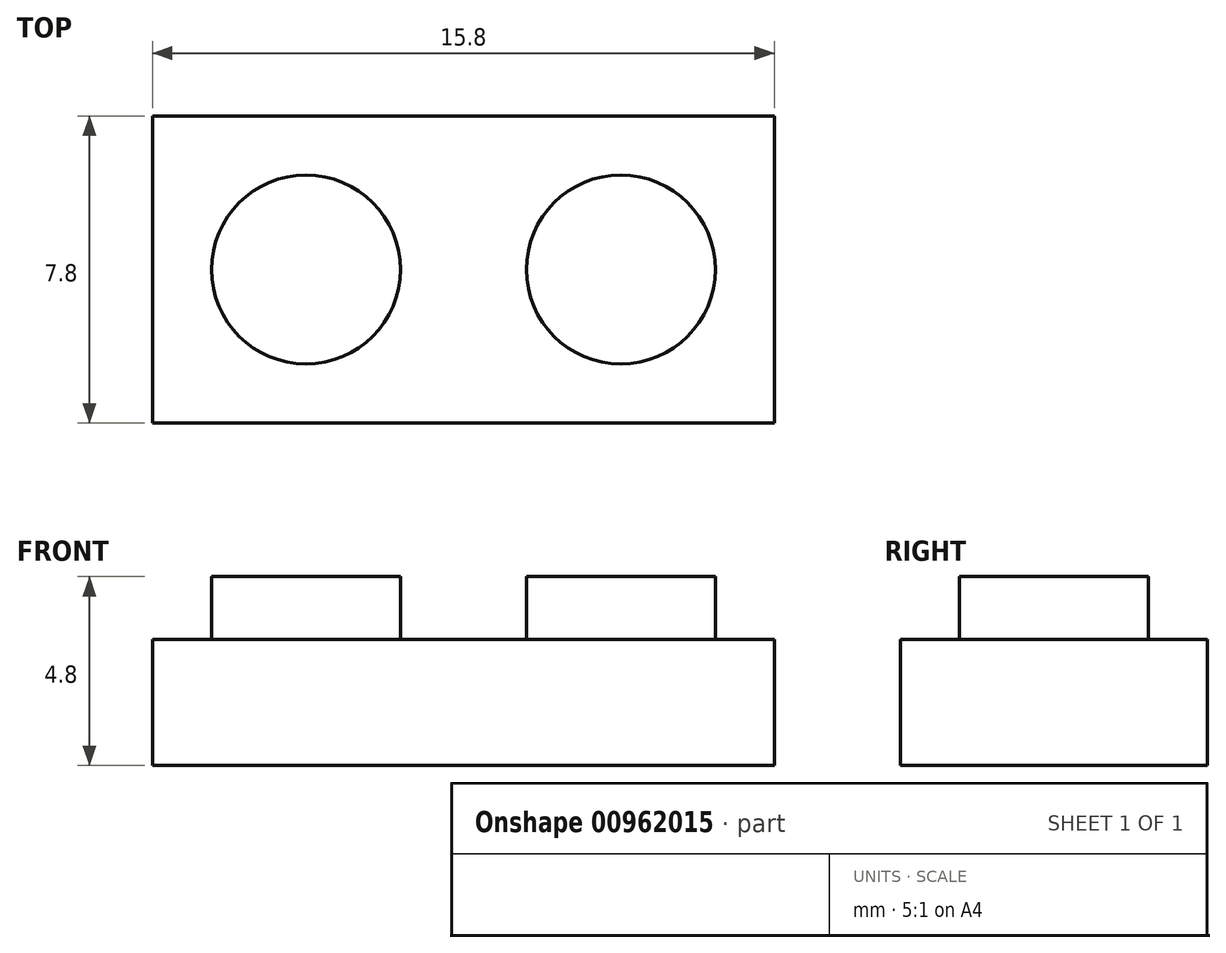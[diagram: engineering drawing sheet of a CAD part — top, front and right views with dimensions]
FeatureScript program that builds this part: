
annotation { "Feature Type Name" : "Feature", "Feature Type Description" : "" }
export const myFeature = defineFeature(function(context is Context, id is Id, definition is map)
    precondition{}
    {
        {
            var Q0;
            Q0=qCreatedBy(makeId("Top.planeOp"),FACE);
            var sketch = newSketch(context, id + "F0", { "sketchPlane" : qUnion([Q0])});
            skLineSegment(sketch, "E0.bottom", {"start": v(7.9, -3.9) * mm, "end": v(-7.9, -3.9) * mm});
            skLineSegment(sketch, "E0.top", {"start": v(7.9, 3.9) * mm, "end": v(-7.9, 3.9) * mm});
            skLineSegment(sketch, "E0.left", {"start": v(7.9, -3.9) * mm, "end": v(7.9, 3.9) * mm});
            skLineSegment(sketch, "E0.right", {"start": v(-7.9, -3.9) * mm, "end": v(-7.9, 3.9) * mm});
            skPoint(sketch, "E0.middle", {"position": v(0, 0) * mm});
            skSolve(sketch);
        }
        {
            var Q0;
            Q0 = qSketchRegion(id + "F0", true);
            extrude(context, id + "F1", {"entities" : qUnion([Q0]), "depth" : 3.2 * mm, "offsetDistance" : 25.4 * mm});
        }
        {
            var Q0;
            Q0=makeQuery(id+"F1.opExtrude","CAP_FACE",FACE,{"disambiguationData":[OSD([sQuery(id+"F0.wireOp",EDGE,"E0.bottom"),sQuery(id+"F0.wireOp",EDGE,"E0.top"),sQuery(id+"F0.wireOp",EDGE,"E0.left"),sQuery(id+"F0.wireOp",EDGE,"E0.right")])],"isStart":false});
            var sketch = newSketch(context, id + "F2", { "sketchPlane" : qUnion([Q0])});
            skLineSegment(sketch, "E1", {"start": v(-7.9, 0) * mm, "end": v(7.9, 0) * mm, "construction": true});
            skCircle(sketch, "E2", {"center": v(-4, 0) * mm, "radius": 2.4 * mm});
            skLineSegment(sketch, "E3", {"start": v(0, 3.9) * mm, "end": v(0, -3.9) * mm, "construction": true});
            skCircle(sketch, "E4.MirrorC", {"center": v(4, 0) * mm, "radius": 2.4 * mm});
            skSolve(sketch);
        }
        {
            var Q0;
            Q0 = qSketchRegion(id + "F2", true);
            extrude(context, id + "F3", {"entities" : qUnion([Q0]), "operationType" : NewBodyOperationType.ADD, "depth" : 1.6 * mm, "offsetDistance" : 25 * mm});
        }
    });
